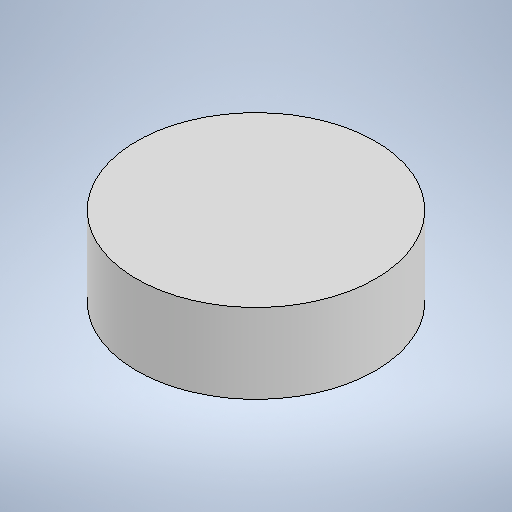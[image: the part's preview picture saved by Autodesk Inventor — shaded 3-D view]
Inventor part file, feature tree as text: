
AUTODESK INVENTOR PART (.ipt)
format: ipt  version: 2025.1 (Build 291241020, 241B)  size: 274,432 bytes
history: native  units: mm
features: sketch x8, extrude x1, revolve x1
ambient origin geometry x8: Origin, YZ Plane, XZ Plane, XY Plane, X Axis, Y Axis, Z Axis, Center Point
bodies: Solid1 (feature_tree)
feature tree (10):
  sketch  "Sketch1"  dims[d0=88.9mm d1=3.0mm]
  sketch  "Sketch2"  dims[d7=120.0mm d9=360.0deg]
  extrude  "Extrusion1"  Depth=3.0mm
  revolve  "Revolution1"  Angle=360.0deg
  sketch  "Sketch Circular Pattern1"  dims[d2=1200.0mm d3=120.0mm d5=360.0deg]
  sketch  "Sketch Circular Pattern2"  dims[d11=200.0mm]
  sketch  "Sketch Circular Pattern3"  dims[d12=120.0mm d14=360.0deg]
  sketch  "Sketch Circular Pattern4"  dims[d20=15.0deg]
  sketch  "Sketch3"  dims[d16=40.0mm d18=360.0deg]
  sketch  "Sketch4"  dims[d21=0.0mm d22=15.0deg d23=45.0deg d24=140.0mm d25=300.0mm d26=460.0mm d27=560.0mm d28=30.0mm d29=10.0mm d30=0.0mm d31=6.0mm d32=1803.421613mm d33=1200.0mm d37=100.0mm d38=30.0mm d39=1200.0mm d40=6.0mm d41=1200.0mm d42=253.289193mm d43=90.0deg]
